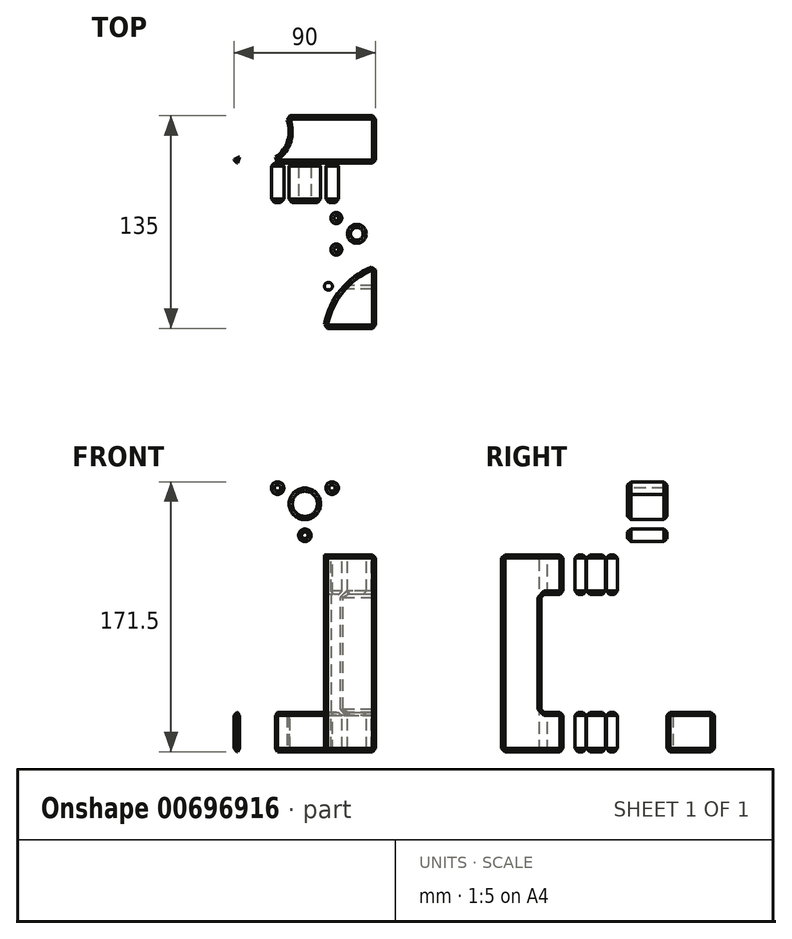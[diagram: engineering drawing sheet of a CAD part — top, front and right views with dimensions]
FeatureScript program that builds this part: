
annotation { "Feature Type Name" : "Feature", "Feature Type Description" : "" }
export const myFeature = defineFeature(function(context is Context, id is Id, definition is map)
    precondition{}
    {
        {
            var Q0;
            Q0=qCreatedBy(makeId("Right.planeOp"),FACE);
            var sketch = newSketch(context, id + "F0", { "sketchPlane" : qUnion([Q0])});
            skLineSegment(sketch, "E0", {"start": v(-98.34, 0) * mm, "end": v(102.1, 0) * mm, "construction": true});
            skLineSegment(sketch, "E1", {"start": v(0, 81.07) * mm, "end": v(0, -100.18) * mm, "construction": true});
            skLineSegment(sketch, "E2", {"start": v(65, -65) * mm, "end": v(-45, -65) * mm});
            skLineSegment(sketch, "E3", {"start": v(-45, -65) * mm, "end": v(-45, 10) * mm});
            skLineSegment(sketch, "E4", {"start": v(-45, 10) * mm, "end": v(35, 10) * mm});
            skLineSegment(sketch, "E5", {"start": v(35, 10) * mm, "end": v(35, 160) * mm});
            skLineSegment(sketch, "E6.0", {"start": v(10, 35) * mm, "end": v(10, 160) * mm});
            skLineSegment(sketch, "E6.1", {"start": v(-70, 35) * mm, "end": v(10, 35) * mm});
            skLineSegment(sketch, "E6.2", {"start": v(-70, -90) * mm, "end": v(-70, 35) * mm});
            skLineSegment(sketch, "E6.3", {"start": v(65, -90) * mm, "end": v(-70, -90) * mm});
            skLineSegment(sketch, "E7", {"start": v(10, 160) * mm, "end": v(35, 160) * mm});
            skLineSegment(sketch, "E8", {"start": v(65, -90) * mm, "end": v(65, -65) * mm});
            skSolve(sketch);
        }
        {
            var Q0;
            Q0 = qSketchRegion(id + "F0", true);
            extrude(context, id + "F1", {"entities" : qUnion([Q0]), "depth" : 45 * mm, "offsetDistance" : 25 * mm, "hasSecondDirection" : true, "secondDirectionOppositeDirection" : true, "secondDirectionDepth" : 45 * mm});
        }
        {
            var Q0;
            Q0=makeQuery(id+"F1.opExtrude","SWEPT_FACE",FACE,{"disambiguationData":[OSD([sQuery(id+"F0.wireOp",EDGE,"E6.0")])]});
            var sketch = newSketch(context, id + "F2", { "sketchPlane" : qUnion([Q0])});
            skLineSegment(sketch, "E9", {"start": v(-94.5, 97.5) * mm, "end": v(109.8, 97.5) * mm, "construction": true});
            skPoint(sketch, "E9.startSnap0", {"position": v(-45, 97.5) * mm});
            skLineSegment(sketch, "E10", {"start": v(0, 170.22) * mm, "end": v(0, 18.97) * mm, "construction": true});
            skPoint(sketch, "E10.startSnap0", {"position": v(0, 160) * mm});
            skPoint(sketch, "E10.endSnap0", {"position": v(0, 35) * mm});
            skCircle(sketch, "E11", {"center": v(0, 127.5) * mm, "radius": 10 * mm});
            skCircle(sketch, "E12", {"center": v(0, 147.5) * mm, "radius": 4 * mm});
            skLineSegment(sketch, "E13", {"start": v(-57.82, 127.5) * mm, "end": v(73.4, 127.5) * mm, "construction": true});
            skCircle(sketch, "E14.1.0", {"center": v(-17.32, 117.5) * mm, "radius": 4 * mm});
            skCircle(sketch, "E14.2.0", {"center": v(17.32, 117.5) * mm, "radius": 4 * mm});
            skCircle(sketch, "E15.MirrorC", {"center": v(17.32, 77.5) * mm, "radius": 4 * mm});
            skCircle(sketch, "E16.MirrorC", {"center": v(-17.32, 77.5) * mm, "radius": 4 * mm});
            skCircle(sketch, "E17.MirrorC", {"center": v(0, 47.5) * mm, "radius": 4 * mm});
            skCircle(sketch, "E18.MirrorC", {"center": v(0, 67.5) * mm, "radius": 10 * mm});
            skLineSegment(sketch, "E19.0", {"start": v(-45, 97.5) * mm, "end": v(-45, 160) * mm});
            skLineSegment(sketch, "E19.1", {"start": v(45, 160) * mm, "end": v(-45, 160) * mm});
            skLineSegment(sketch, "E19.2", {"start": v(45, 97.5) * mm, "end": v(45, 160) * mm});
            skArc(sketch, "E20", {"start": v(32.5, 127.5) * mm, "mid": v(0, 160) * mm, "end": v(-32.5, 127.5) * mm});
            skArc(sketch, "E21", {"start": v(32.5, 127.5) * mm, "mid": v(35.95, 111.33) * mm, "end": v(45, 97.5) * mm});
            skArc(sketch, "E22", {"start": v(-45, 97.5) * mm, "mid": v(-35.95, 111.33) * mm, "end": v(-32.5, 127.5) * mm});
            skLineSegment(sketch, "E23", {"start": v(-32.5, 127.5) * mm, "end": v(-45, 97.5) * mm, "construction": true});
            skLineSegment(sketch, "E24", {"start": v(45, 97.5) * mm, "end": v(32.5, 127.5) * mm, "construction": true});
            skSolve(sketch);
        }
        {
            var Q0;
            {var subQ0=sQuery(id+"F2.wireOp",EDGE,"E19.0");Q0=makeQuery(id+"F2.imprint","IMPRINT",FACE,{"disambiguationData":[TD([[makeQuery(id+"F2.imprint","IMPRINT",EDGE,{"derivedFrom":subQ0}),-1.0]])]});}
            var Q1;
            {var subQ0=sQuery(id+"F2.wireOp",EDGE,"E19.2");Q1=makeQuery(id+"F2.imprint","IMPRINT",FACE,{"disambiguationData":[TD([[makeQuery(id+"F2.imprint","IMPRINT",EDGE,{"derivedFrom":subQ0}),1.0]])]});}
            var Q2;
            Q2=makeQuery(id+"F2.imprint","IMPRINT",FACE,{"disambiguationData":[TD([[makeQuery(id+"F2.imprint","IMPRINT",EDGE,{"derivedFrom":sQuery(id+"F2.wireOp",EDGE,"E11")}),1.0]])]});
            var Q3;
            Q3=makeQuery(id+"F2.imprint","IMPRINT",FACE,{"disambiguationData":[TD([[makeQuery(id+"F2.imprint","IMPRINT",EDGE,{"derivedFrom":sQuery(id+"F2.wireOp",EDGE,"E12")}),1.0]])]});
            var Q4;
            Q4=makeQuery(id+"F2.imprint","IMPRINT",FACE,{"disambiguationData":[TD([[makeQuery(id+"F2.imprint","IMPRINT",EDGE,{"derivedFrom":sQuery(id+"F2.wireOp",EDGE,"E14.2.0")}),1.0]])]});
            var Q5;
            Q5=makeQuery(id+"F2.imprint","IMPRINT",FACE,{"disambiguationData":[TD([[makeQuery(id+"F2.imprint","IMPRINT",EDGE,{"derivedFrom":sQuery(id+"F2.wireOp",EDGE,"E14.1.0")}),1.0]])]});
            var Q6;
            Q6=makeQuery(id+"F2.imprint","IMPRINT",FACE,{"disambiguationData":[TD([[makeQuery(id+"F2.imprint","IMPRINT",EDGE,{"derivedFrom":sQuery(id+"F2.wireOp",EDGE,"E18.MirrorC")}),-1.0]])]});
            var Q7;
            Q7=makeQuery(id+"F2.imprint","IMPRINT",FACE,{"disambiguationData":[TD([[makeQuery(id+"F2.imprint","IMPRINT",EDGE,{"derivedFrom":sQuery(id+"F2.wireOp",EDGE,"E15.MirrorC")}),-1.0]])]});
            var Q8;
            Q8=makeQuery(id+"F2.imprint","IMPRINT",FACE,{"disambiguationData":[TD([[makeQuery(id+"F2.imprint","IMPRINT",EDGE,{"derivedFrom":sQuery(id+"F2.wireOp",EDGE,"E16.MirrorC")}),-1.0]])]});
            var Q9;
            Q9=makeQuery(id+"F2.imprint","IMPRINT",FACE,{"disambiguationData":[TD([[makeQuery(id+"F2.imprint","IMPRINT",EDGE,{"derivedFrom":sQuery(id+"F2.wireOp",EDGE,"E17.MirrorC")}),-1.0]])]});
            var Q10;
            Q10=makeQuery(id+"F1.opExtrude","SWEPT_FACE",FACE,{"disambiguationData":[OSD([sQuery(id+"F0.wireOp",EDGE,"E5")])]});
            extrude(context, id + "F3", {"entities" : qUnion([Q0, Q1, Q2, Q3, Q4, Q5, Q6, Q7, Q8, Q9]), "operationType" : NewBodyOperationType.REMOVE, "endBound" : BoundingType.UP_TO_SURFACE, "oppositeDirection" : true, "depth" : 25 * mm, "endBoundEntityFace" : qUnion([Q10]), "offsetDistance" : 25 * mm});
        }
        {
            var Q0;
            Q0=makeQuery(id+"F1.opExtrude","SWEPT_FACE",FACE,{"disambiguationData":[OSD([sQuery(id+"F0.wireOp",EDGE,"E6.1")])]});
            var sketch = newSketch(context, id + "F4", { "sketchPlane" : qUnion([Q0])});
            skLineSegment(sketch, "E25.0", {"start": v(-45, -70) * mm, "end": v(-45, 10) * mm});
            skLineSegment(sketch, "E25.1", {"start": v(45, -70) * mm, "end": v(-45, -70) * mm});
            skLineSegment(sketch, "E25.2", {"start": v(45, -70) * mm, "end": v(45, 10) * mm});
            skLineSegment(sketch, "E26", {"start": v(0, -82.71) * mm, "end": v(0, 86.88) * mm, "construction": true});
            skPoint(sketch, "E26.startSnap0", {"position": v(0, -70) * mm});
            skLineSegment(sketch, "E27", {"start": v(-54.33, -30) * mm, "end": v(58.26, -30) * mm, "construction": true});
            skPoint(sketch, "E27.startSnap0", {"position": v(-45, -30) * mm});
            skPoint(sketch, "E27.endSnap0", {"position": v(45, -30) * mm});
            skLineSegment(sketch, "E28", {"start": v(0, -70) * mm, "end": v(-12, -70) * mm});
            skArc(sketch, "E29", {"start": v(-12, -70) * mm, "mid": v(-22.9, -45.39) * mm, "end": v(-45, -30) * mm});
            skCircle(sketch, "E30", {"center": v(-33, -10) * mm, "radius": 6 * mm});
            skCircle(sketch, "E31", {"center": v(-20, -20) * mm, "radius": 3.5 * mm});
            skCircle(sketch, "E32", {"center": v(-20, 0) * mm, "radius": 3.5 * mm});
            skLineSegment(sketch, "E33", {"start": v(-45, -70) * mm, "end": v(0, -30) * mm, "construction": true});
            skLineSegment(sketch, "E34", {"start": v(-45, -30) * mm, "end": v(-12, -70) * mm, "construction": true});
            skCircle(sketch, "E35", {"center": v(-15, -43.33) * mm, "radius": 2.5 * mm});
            skCircle(sketch, "E36.MirrorC", {"center": v(33, -10) * mm, "radius": 6 * mm});
            skArc(sketch, "E37.MirrorCS", {"start": v(12, -70) * mm, "mid": v(22.9, -45.39) * mm, "end": v(45, -30) * mm});
            skCircle(sketch, "E38.MirrorC", {"center": v(20, -20) * mm, "radius": 3.5 * mm});
            skCircle(sketch, "E39.MirrorC", {"center": v(20, 0) * mm, "radius": 3.5 * mm});
            skLineSegment(sketch, "E40.MirrorCS", {"start": v(45, -30) * mm, "end": v(12, -70) * mm, "construction": true});
            skCircle(sketch, "E41.MirrorC", {"center": v(15, -43.33) * mm, "radius": 2.5 * mm});
            skLineSegment(sketch, "E42.MirrorCS", {"start": v(45, -70) * mm, "end": v(0, -30) * mm, "construction": true});
            skSolve(sketch);
        }
        {
            var Q0;
            {var subQ3=sQuery(id+"F4.wireOp",EDGE,"E29");Q0=makeQuery(id+"F4.imprint","IMPRINT",FACE,{"disambiguationData":[TD([[makeQuery(id+"F4.imprint","IMPRINT",EDGE,{"derivedFrom":subQ3}),1.0]])]});}
            var Q1;
            {var subQ3=sQuery(id+"F4.wireOp",EDGE,"E37.MirrorCS");Q1=makeQuery(id+"F4.imprint","IMPRINT",FACE,{"disambiguationData":[TD([[makeQuery(id+"F4.imprint","IMPRINT",EDGE,{"derivedFrom":subQ3}),-1.0]])]});}
            var Q2;
            Q2=makeQuery(id+"F4.imprint","IMPRINT",FACE,{"disambiguationData":[TD([[makeQuery(id+"F4.imprint","IMPRINT",EDGE,{"derivedFrom":sQuery(id+"F4.wireOp",EDGE,"E36.MirrorC")}),-1.0]])]});
            var Q3;
            Q3=makeQuery(id+"F4.imprint","IMPRINT",FACE,{"disambiguationData":[TD([[makeQuery(id+"F4.imprint","IMPRINT",EDGE,{"derivedFrom":sQuery(id+"F4.wireOp",EDGE,"E38.MirrorC")}),-1.0]])]});
            var Q4;
            Q4=makeQuery(id+"F4.imprint","IMPRINT",FACE,{"disambiguationData":[TD([[makeQuery(id+"F4.imprint","IMPRINT",EDGE,{"derivedFrom":sQuery(id+"F4.wireOp",EDGE,"E41.MirrorC")}),-1.0]])]});
            var Q5;
            Q5=makeQuery(id+"F4.imprint","IMPRINT",FACE,{"disambiguationData":[TD([[makeQuery(id+"F4.imprint","IMPRINT",EDGE,{"derivedFrom":sQuery(id+"F4.wireOp",EDGE,"E35")}),1.0]])]});
            var Q6;
            Q6=makeQuery(id+"F4.imprint","IMPRINT",FACE,{"disambiguationData":[TD([[makeQuery(id+"F4.imprint","IMPRINT",EDGE,{"derivedFrom":sQuery(id+"F4.wireOp",EDGE,"E31")}),1.0]])]});
            var Q7;
            Q7=makeQuery(id+"F4.imprint","IMPRINT",FACE,{"disambiguationData":[TD([[makeQuery(id+"F4.imprint","IMPRINT",EDGE,{"derivedFrom":sQuery(id+"F4.wireOp",EDGE,"E30")}),1.0]])]});
            var Q8;
            Q8=makeQuery(id+"F4.imprint","IMPRINT",FACE,{"disambiguationData":[TD([[makeQuery(id+"F4.imprint","IMPRINT",EDGE,{"derivedFrom":sQuery(id+"F4.wireOp",EDGE,"E32")}),1.0]])]});
            var Q9;
            Q9=makeQuery(id+"F4.imprint","IMPRINT",FACE,{"disambiguationData":[TD([[makeQuery(id+"F4.imprint","IMPRINT",EDGE,{"derivedFrom":sQuery(id+"F4.wireOp",EDGE,"E39.MirrorC")}),-1.0]])]});
            var Q10;
            Q10=makeQuery(id+"F1.opExtrude","SWEPT_FACE",FACE,{"disambiguationData":[OSD([sQuery(id+"F0.wireOp",EDGE,"E6.3")])]});
            extrude(context, id + "F5", {"entities" : qUnion([Q0, Q1, Q2, Q3, Q4, Q5, Q6, Q7, Q8, Q9]), "operationType" : NewBodyOperationType.REMOVE, "endBound" : BoundingType.UP_TO_SURFACE, "oppositeDirection" : true, "depth" : 25 * mm, "endBoundEntityFace" : qUnion([Q10]), "offsetDistance" : 25 * mm});
        }
        {
            var Q0;
            Q0=makeQuery(id+"F1.opExtrude","SWEPT_FACE",FACE,{"disambiguationData":[OSD([sQuery(id+"F0.wireOp",EDGE,"E6.3")])]});
            var sketch = newSketch(context, id + "F6", { "sketchPlane" : qUnion([Q0])});
            skLineSegment(sketch, "E43", {"start": v(0, -78.31) * mm, "end": v(0, 96.08) * mm, "construction": true});
            skPoint(sketch, "E43.startSnap0", {"position": v(0, -65) * mm});
            skCircle(sketch, "E44", {"center": v(-30, -55) * mm, "radius": 20 * mm});
            skLineSegment(sketch, "E45.0", {"start": v(-45, -25) * mm, "end": v(-45, -15) * mm});
            skLineSegment(sketch, "E46.bottom", {"start": v(-45, -25) * mm, "end": v(-30, -25) * mm});
            skLineSegment(sketch, "E46.top", {"start": v(-45, -15) * mm, "end": v(-30, -15) * mm});
            skLineSegment(sketch, "E46.right", {"start": v(-30, -25) * mm, "end": v(-30, -15) * mm});
            skLineSegment(sketch, "E47.MirrorCS", {"start": v(45, -25) * mm, "end": v(45, -15) * mm});
            skCircle(sketch, "E48.MirrorC", {"center": v(30, -55) * mm, "radius": 20 * mm});
            skLineSegment(sketch, "E49.MirrorCS", {"start": v(45, -25) * mm, "end": v(30, -25) * mm});
            skLineSegment(sketch, "E50.MirrorCS", {"start": v(30, -25) * mm, "end": v(30, -15) * mm});
            skLineSegment(sketch, "E51.MirrorCS", {"start": v(45, -15) * mm, "end": v(30, -15) * mm});
            skSolve(sketch);
        }
        {
            var Q0;
            {var subQ0=sQuery(id+"F6.wireOp",EDGE,"E44");var subQ1=sQuery(id+"F0.wireOp",EDGE,"E6.3");var subQ4=makeQuery(id+"F1.opExtrude","CAP_EDGE",EDGE,{"disambiguationData":[OSD([subQ1])],"isStart":true});var subQ5=makeQuery(id+"F6.imprint","INTERSECT",VERTEX,{"derivedFrom":[subQ4,subQ0]});Q0=makeQuery(id+"F6.imprint","IMPRINT",FACE,{"disambiguationData":[TD([[makeQuery(id+"F6.imprint","IMPRINT",EDGE,{"disambiguationData":[TD([[subQ5,1.0]])],"derivedFrom":subQ0}),1.0]])]});}
            var Q1;
            {var subQ0=sQuery(id+"F6.wireOp",EDGE,"E48.MirrorC");var subQ1=sQuery(id+"F0.wireOp",EDGE,"E6.3");var subQ4=makeQuery(id+"F1.opExtrude","CAP_EDGE",EDGE,{"disambiguationData":[OSD([subQ1])],"isStart":false});var subQ5=makeQuery(id+"F6.imprint","INTERSECT",VERTEX,{"derivedFrom":[subQ4,subQ0]});Q1=makeQuery(id+"F6.imprint","IMPRINT",FACE,{"disambiguationData":[TD([[makeQuery(id+"F6.imprint","IMPRINT",EDGE,{"disambiguationData":[TD([[subQ5,1.0]])],"derivedFrom":subQ0}),-1.0]])]});}
            var Q2;
            Q2=makeQuery(id+"F6.imprint","IMPRINT",FACE,{"disambiguationData":[TD([[makeQuery(id+"F6.imprint","IMPRINT",EDGE,{"derivedFrom":sQuery(id+"F6.wireOp",EDGE,"E47.MirrorCS")}),1.0]])]});
            var Q3;
            Q3=makeQuery(id+"F6.imprint","IMPRINT",FACE,{"disambiguationData":[TD([[makeQuery(id+"F6.imprint","IMPRINT",EDGE,{"derivedFrom":sQuery(id+"F6.wireOp",EDGE,"E46.bottom")}),1.0]])]});
            var Q4;
            Q4=makeQuery(id+"F1.opExtrude","SWEPT_FACE",FACE,{"disambiguationData":[OSD([sQuery(id+"F0.wireOp",EDGE,"E2")])]});
            extrude(context, id + "F7", {"entities" : qUnion([Q0, Q1, Q2, Q3]), "operationType" : NewBodyOperationType.REMOVE, "endBound" : BoundingType.UP_TO_SURFACE, "oppositeDirection" : true, "depth" : 25 * mm, "endBoundEntityFace" : qUnion([Q4]), "offsetDistance" : 25 * mm});
        }
        {
            var Q0;
            Q0=makeQuery(id+"F1.opExtrude","SWEPT_FACE",FACE,{"disambiguationData":[OSD([sQuery(id+"F0.wireOp",EDGE,"E6.0")])]});
            var Q1;
            Q1=makeQuery(id+"F5.boolean.opBoolean","COPY",FACE,{"derivedFrom":makeQuery(id+"F5.opExtrude","SWEPT_FACE",FACE,{"disambiguationData":[OSD([sQuery(id+"F4.wireOp",EDGE,"E29")])]})});
            var Q2;
            {var subQ0=sQuery(id+"F0.wireOp",EDGE,"E6.1");var subQ1=sQuery(id+"F0.wireOp",EDGE,"E6.0");var subQ2=sQuery(id+"F0.wireOp",EDGE,"E5");var subQ3=sQuery(id+"F0.wireOp",EDGE,"E4");Q2=makeQuery(id+"F5.boolean.opBoolean","SPLIT",FACE,{"disambiguationData":[TD([makeQuery(id+"F1.opExtrude","SWEPT_FACE",FACE,{"disambiguationData":[OSD([subQ3])]})])],"derivedFrom":makeQuery(id+"F1.opExtrude","CAP_FACE",FACE,{"disambiguationData":[OSD([sQuery(id+"F0.wireOp",EDGE,"E2"),sQuery(id+"F0.wireOp",EDGE,"E3"),subQ3,subQ2,subQ1,subQ0,sQuery(id+"F0.wireOp",EDGE,"E6.2"),sQuery(id+"F0.wireOp",EDGE,"E6.3"),sQuery(id+"F0.wireOp",EDGE,"E7"),sQuery(id+"F0.wireOp",EDGE,"E8")])],"isStart":true})});}
            var Q3;
            Q3=makeQuery(id+"F3.boolean.opBoolean","COPY",FACE,{"derivedFrom":makeQuery(id+"F3.opExtrude","SWEPT_FACE",FACE,{"disambiguationData":[OSD([sQuery(id+"F2.wireOp",EDGE,"E22")])]})});
            var Q4;
            {var subQ0=sQuery(id+"F2.wireOp",EDGE,"E20");Q4=makeQuery(id+"F3.boolean.opBoolean","TWEAK_FACE",FACE,{"derivedFrom":[makeQuery(id+"F3.opExtrude","SWEPT_FACE",FACE,{"disambiguationData":[OSD([subQ0]),TDD([makeQuery(id+"F2.imprint","IMPRINT",EDGE,{"disambiguationData":[TD([[makeQuery(id+"F2.imprint","INTERSECT",VERTEX,{"derivedFrom":[subQ0,sQuery(id+"F2.wireOp",EDGE,"E21")]}),-1.0]])],"derivedFrom":subQ0})])]}),makeQuery(id+"F3.opExtrude","SWEPT_FACE",FACE,{"disambiguationData":[OSD([subQ0]),TDD([makeQuery(id+"F2.imprint","IMPRINT",EDGE,{"disambiguationData":[TD([[makeQuery(id+"F2.imprint","INTERSECT",VERTEX,{"derivedFrom":[subQ0,sQuery(id+"F2.wireOp",EDGE,"E22")]}),1.0]])],"derivedFrom":subQ0})])]})]});}
            var Q5;
            Q5=makeQuery(id+"F5.boolean.opBoolean","COPY",FACE,{"derivedFrom":makeQuery(id+"F5.opExtrude","SWEPT_FACE",FACE,{"disambiguationData":[OSD([sQuery(id+"F4.wireOp",EDGE,"E37.MirrorCS")])]})});
            var Q6;
            {var subQ0=sQuery(id+"F0.wireOp",EDGE,"E6.1");var subQ1=sQuery(id+"F0.wireOp",EDGE,"E6.0");var subQ2=sQuery(id+"F0.wireOp",EDGE,"E5");var subQ3=sQuery(id+"F0.wireOp",EDGE,"E4");Q6=makeQuery(id+"F5.boolean.opBoolean","SPLIT",FACE,{"disambiguationData":[TD([makeQuery(id+"F1.opExtrude","SWEPT_FACE",FACE,{"disambiguationData":[OSD([subQ3])]})])],"derivedFrom":makeQuery(id+"F1.opExtrude","CAP_FACE",FACE,{"disambiguationData":[OSD([sQuery(id+"F0.wireOp",EDGE,"E2"),sQuery(id+"F0.wireOp",EDGE,"E3"),subQ3,subQ2,subQ1,subQ0,sQuery(id+"F0.wireOp",EDGE,"E6.2"),sQuery(id+"F0.wireOp",EDGE,"E6.3"),sQuery(id+"F0.wireOp",EDGE,"E7"),sQuery(id+"F0.wireOp",EDGE,"E8")])],"isStart":false})});}
            var Q7;
            Q7=makeQuery(id+"F1.opExtrude","SWEPT_FACE",FACE,{"disambiguationData":[OSD([sQuery(id+"F0.wireOp",EDGE,"E6.1")])]});
            var Q8;
            Q8=makeQuery(id+"F1.opExtrude","SWEPT_FACE",FACE,{"disambiguationData":[OSD([sQuery(id+"F0.wireOp",EDGE,"E2")])]});
            var Q9;
            {var subQ0=sQuery(id+"F0.wireOp",EDGE,"E2");var subQ1=makeQuery(id+"F1.opExtrude","SWEPT_FACE",FACE,{"disambiguationData":[OSD([subQ0])]});var subQ2=makeQuery(id+"F5.opExtrude","SWEPT_FACE",FACE,{"disambiguationData":[OSD([sQuery(id+"F4.wireOp",EDGE,"E37.MirrorCS")])]});var subQ3=sQuery(id+"F0.wireOp",EDGE,"E6.3");var subQ5=sQuery(id+"F0.wireOp",EDGE,"E8");Q9=makeQuery(id+"F7.boolean.opBoolean","SPLIT",FACE,{"disambiguationData":[TD([makeQuery(id+"F5.boolean.opBoolean","COPY",FACE,{"derivedFrom":subQ2})])],"derivedFrom":makeQuery(id+"F5.boolean.opBoolean","SPLIT",FACE,{"disambiguationData":[TD([subQ1])],"derivedFrom":makeQuery(id+"F1.opExtrude","CAP_FACE",FACE,{"disambiguationData":[OSD([subQ0,sQuery(id+"F0.wireOp",EDGE,"E3"),sQuery(id+"F0.wireOp",EDGE,"E4"),sQuery(id+"F0.wireOp",EDGE,"E5"),sQuery(id+"F0.wireOp",EDGE,"E6.0"),sQuery(id+"F0.wireOp",EDGE,"E6.1"),sQuery(id+"F0.wireOp",EDGE,"E6.2"),subQ3,sQuery(id+"F0.wireOp",EDGE,"E7"),subQ5])],"isStart":false})})});}
            var Q10;
            {var subQ0=sQuery(id+"F0.wireOp",EDGE,"E6.3");Q10=makeQuery(id+"F7.boolean.opBoolean","SPLIT",EDGE,{"disambiguationData":[TD([makeQuery(id+"F7.opExtrude","SWEPT_FACE",FACE,{"disambiguationData":[OSD([sQuery(id+"F6.wireOp",EDGE,"E48.MirrorC")])]})])],"derivedFrom":makeQuery(id+"F1.opExtrude","CAP_EDGE",EDGE,{"disambiguationData":[OSD([subQ0])],"isStart":false})});}
            var Q11;
            {var subQ0=sQuery(id+"F0.wireOp",EDGE,"E2");var subQ1=makeQuery(id+"F1.opExtrude","SWEPT_FACE",FACE,{"disambiguationData":[OSD([subQ0])]});var subQ2=sQuery(id+"F0.wireOp",EDGE,"E6.3");var subQ4=sQuery(id+"F0.wireOp",EDGE,"E8");Q11=makeQuery(id+"F7.boolean.opBoolean","SPLIT",FACE,{"disambiguationData":[TD([makeQuery(id+"F7.opExtrude","SWEPT_FACE",FACE,{"disambiguationData":[OSD([sQuery(id+"F6.wireOp",EDGE,"E48.MirrorC")])]})])],"derivedFrom":makeQuery(id+"F5.boolean.opBoolean","SPLIT",FACE,{"disambiguationData":[TD([subQ1])],"derivedFrom":makeQuery(id+"F1.opExtrude","CAP_FACE",FACE,{"disambiguationData":[OSD([subQ0,sQuery(id+"F0.wireOp",EDGE,"E3"),sQuery(id+"F0.wireOp",EDGE,"E4"),sQuery(id+"F0.wireOp",EDGE,"E5"),sQuery(id+"F0.wireOp",EDGE,"E6.0"),sQuery(id+"F0.wireOp",EDGE,"E6.1"),sQuery(id+"F0.wireOp",EDGE,"E6.2"),subQ2,sQuery(id+"F0.wireOp",EDGE,"E7"),subQ4])],"isStart":false})})});}
            var Q12;
            Q12=makeQuery(id+"F7.boolean.opBoolean","COPY",FACE,{"derivedFrom":makeQuery(id+"F7.opExtrude","SWEPT_FACE",FACE,{"disambiguationData":[OSD([sQuery(id+"F6.wireOp",EDGE,"E48.MirrorC")])]})});
            var Q13;
            Q13=makeQuery(id+"F1.opExtrude","SWEPT_FACE",FACE,{"disambiguationData":[OSD([sQuery(id+"F0.wireOp",EDGE,"E8")])]});
            var Q14;
            Q14=makeQuery(id+"F7.boolean.opBoolean","COPY",EDGE,{"derivedFrom":makeQuery(id+"F7.opExtrude","CAP_EDGE",EDGE,{"disambiguationData":[OSD([sQuery(id+"F6.wireOp",EDGE,"E44")])],"isStart":true})});
            var Q15;
            Q15=makeQuery(id+"F7.boolean.opBoolean","COPY",FACE,{"derivedFrom":makeQuery(id+"F7.opExtrude","SWEPT_FACE",FACE,{"disambiguationData":[OSD([sQuery(id+"F6.wireOp",EDGE,"E44")])]})});
            var Q16;
            Q16=makeQuery(id+"F1.opExtrude","SWEPT_FACE",FACE,{"disambiguationData":[OSD([sQuery(id+"F0.wireOp",EDGE,"E6.3")])]});
            var Q17;
            Q17=makeQuery(id+"F1.opExtrude","SWEPT_FACE",FACE,{"disambiguationData":[OSD([sQuery(id+"F0.wireOp",EDGE,"E4")])]});
            var Q18;
            Q18=makeQuery(id+"F1.opExtrude","SWEPT_FACE",FACE,{"disambiguationData":[OSD([sQuery(id+"F0.wireOp",EDGE,"E5")])]});
            chamfer(context, id + "F8", {"entities" : qUnion([Q0, Q1, Q2, Q3, Q4, Q5, Q6, Q7, Q8, Q9, Q10, Q11, Q12, Q13, Q14, Q15, Q16, Q17, Q18]), "width" : 2 * mm, "tangentPropagation" : true});
        }
    });
